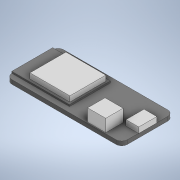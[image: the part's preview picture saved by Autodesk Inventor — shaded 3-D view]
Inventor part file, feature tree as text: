
AUTODESK INVENTOR PART (.ipt)
format: ipt  version: 2020 (Build 240168000, 168)  size: 166,912 bytes
history: native  units: in
note: dims shown in document units (in); Inventor stores cm internally (conversion verified against a paired STEP export)
features: extrude x6, other x1, fillet x1
ambient origin geometry x8: Origin, YZ Plane, XZ Plane, XY Plane, X Axis, Y Axis, Z Axis, Center Point
bodies: Solid1 (feature_tree)
feature tree (8):
  other  "ESP32 Feather"
  extrude  "PCB"  Depth=2.0079in
  fillet  "Fillet1"  Radius=0.0709in
  extrude  "ESP32PCB"  Depth=0.0295in
  extrude  "ESP32Shied"  Depth=1.0039in
  extrude  "Battery Connector"  Depth=0.6949in
  extrude  "Extrusion5"  Depth=0.0925in
  extrude  "Extrusion6"  Depth=0.9685in
